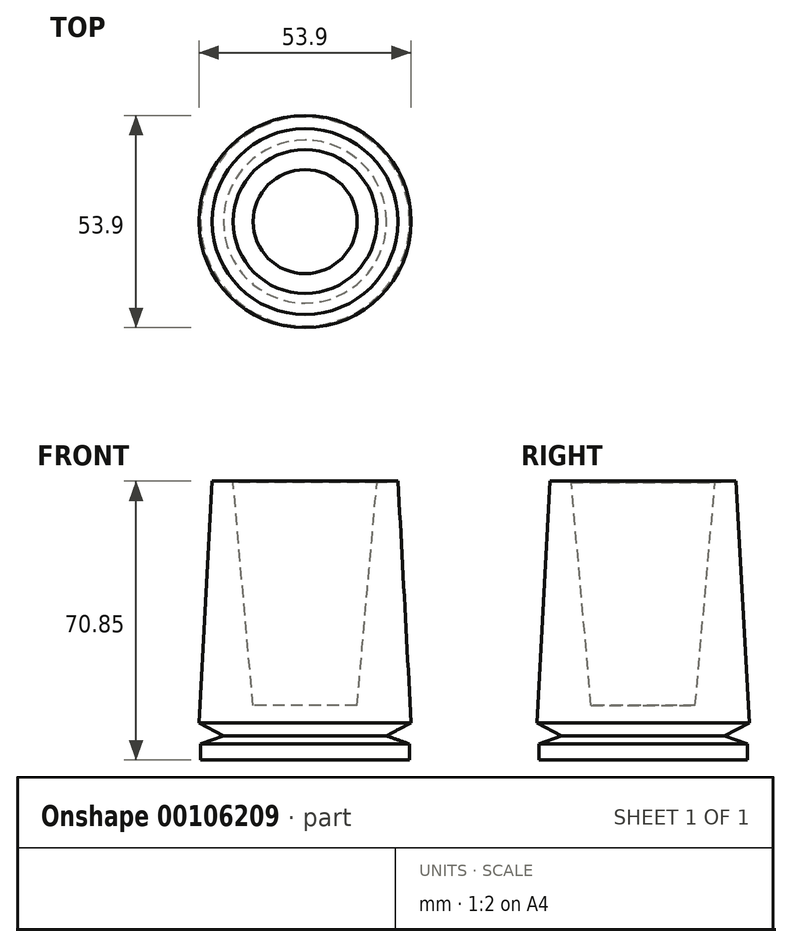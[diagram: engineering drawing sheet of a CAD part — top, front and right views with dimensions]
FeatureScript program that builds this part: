
annotation { "Feature Type Name" : "Feature", "Feature Type Description" : "" }
export const myFeature = defineFeature(function(context is Context, id is Id, definition is map)
    precondition{}
    {
        {
            var Q0;
            Q0=qCreatedBy(makeId("Front.planeOp"),FACE);
            var sketch = newSketch(context, id + "F0", { "sketchPlane" : qUnion([Q0])});
            skLineSegment(sketch, "E0", {"start": v(0, 0) * mm, "end": v(-26.53, 0) * mm});
            skLineSegment(sketch, "E1", {"start": v(-26.53, 0) * mm, "end": v(-26.53, 4.06) * mm});
            skLineSegment(sketch, "E2", {"start": v(-26.53, 4.06) * mm, "end": v(-20.7, 6.14) * mm});
            skLineSegment(sketch, "E3", {"start": v(-20.7, 6.14) * mm, "end": v(-26.95, 9.47) * mm});
            skLineSegment(sketch, "E4", {"start": v(-26.95, 9.47) * mm, "end": v(-23.62, 70.85) * mm});
            skLineSegment(sketch, "E5", {"start": v(-23.62, 70.85) * mm, "end": v(-18.27, 70.56) * mm});
            skLineSegment(sketch, "E6", {"start": v(-18.27, 70.56) * mm, "end": v(-13.21, 13.84) * mm});
            skLineSegment(sketch, "E7", {"start": v(-13.21, 13.84) * mm, "end": v(0, 13.84) * mm});
            skLineSegment(sketch, "E8", {"start": v(0, 13.84) * mm, "end": v(0, 0) * mm});
            skSolve(sketch);
        }
        {
            var Q0;
            Q0=makeQuery(id+"F0.imprint","IMPRINT",FACE,{"disambiguationData":[TD([[makeQuery(id+"F0.imprint","IMPRINT",EDGE,{"derivedFrom":sQuery(id+"F0.wireOp",EDGE,"E0")}),-1.0]])]});
            var Q1;
            Q1=sQuery(id+"F0.wireOp",EDGE,"E8");
            revolve(context, id + "F1", {"entities" : qUnion([Q0]), "axis" : qUnion([Q1]), "revolveType" : RevolveType.FULL});
        }
    });
